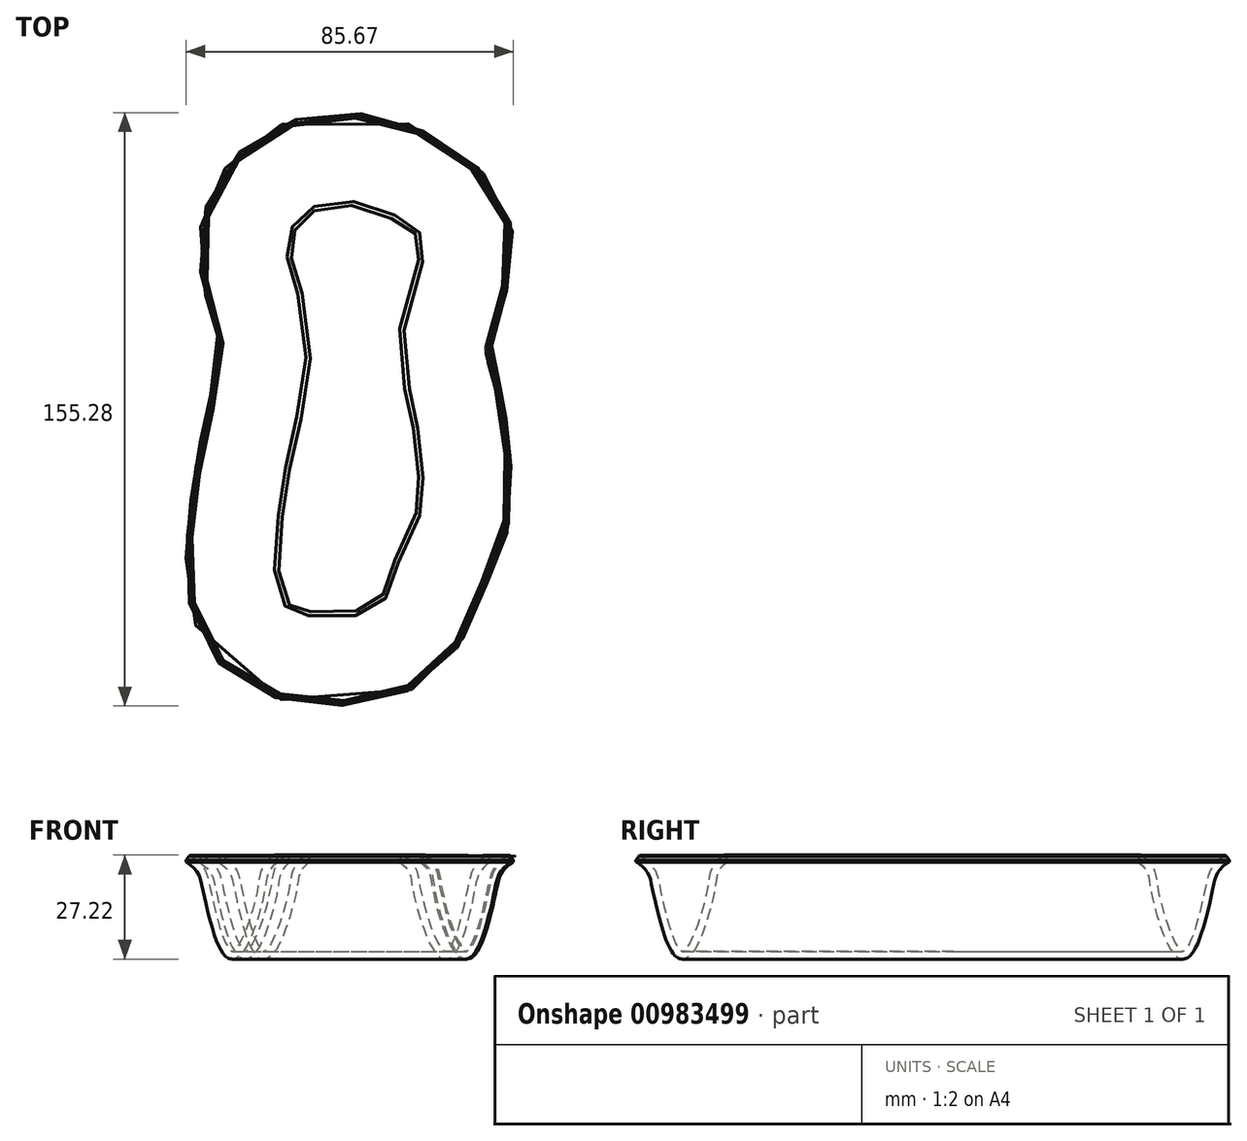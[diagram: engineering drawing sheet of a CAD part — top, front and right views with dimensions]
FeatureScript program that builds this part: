
annotation { "Feature Type Name" : "Feature", "Feature Type Description" : "" }
export const myFeature = defineFeature(function(context is Context, id is Id, definition is map)
    precondition{}
    {
        {
            var Q0;
            Q0=qCreatedBy(makeId("Top.planeOp"),FACE);
            var sketch = newSketch(context, id + "F0", { "sketchPlane" : qUnion([Q0])});
            skFitSpline(sketch, "E0", {"points": [v(28.25, 0) * mm, v(26.64, 14.63) * mm, v(31.87, 37.77) * mm, v(21.57, 52.86) * mm, v(0, 60) * mm, v(-19.3, 52.86) * mm, v(-26, 34.83) * mm, v(-21.77, 16.91) * mm, v(-22.37, 0) * mm, v(-26.08, -17.1) * mm, v(-28.78, -35.26) * mm, v(-27.37, -58.36) * mm, v(-12.12, -70) * mm, v(15, -66) * mm, v(24.45, -49.5) * mm, v(30.66, -34.33) * mm, v(30.66, -13.46) * mm, v(28.25, 0) * mm]});
            skFitSpline(sketch, "E1.0", {"points": [v(40.04, 2.28) * mm, v(39.9, 2.84) * mm, v(39.78, 3.38) * mm, v(39.6, 4.08) * mm, v(39.4, 4.9) * mm, v(39.17, 5.83) * mm, v(38.9, 7) * mm, v(38.64, 8.3) * mm, v(38.44, 9.68) * mm, v(38.38, 10.72) * mm, v(38.39, 11.53) * mm, v(38.42, 12.04) * mm, v(38.46, 12.45) * mm, v(38.5, 12.76) * mm, v(38.55, 13.08) * mm, v(38.61, 13.46) * mm, v(38.7, 13.87) * mm, v(38.83, 14.47) * mm, v(39.12, 15.64) * mm, v(39.7, 17.61) * mm, v(40.57, 20.35) * mm, v(41.54, 23.39) * mm, v(42.33, 26.16) * mm, v(42.91, 28.53) * mm, v(43.3, 30.39) * mm, v(43.62, 32.34) * mm, v(43.8, 34.06) * mm, v(43.88, 35.49) * mm, v(43.91, 36.58) * mm, v(43.9, 37.52) * mm, v(43.86, 38.29) * mm, v(43.81, 39.06) * mm, v(43.72, 40.02) * mm, v(43.5, 41.54) * mm, v(43.11, 43.4) * mm, v(42.47, 45.53) * mm, v(41.68, 47.57) * mm, v(40.76, 49.5) * mm, v(39.37, 51.91) * mm, v(37.41, 54.65) * mm, v(34.8, 57.53) * mm, v(32.03, 60.05) * mm, v(29.62, 61.9) * mm, v(27.66, 63.24) * mm, v(26.16, 64.2) * mm, v(24.61, 65.12) * mm, v(22.5, 66.28) * mm, v(19.8, 67.6) * mm, v(15.28, 69.43) * mm, v(10.53, 70.82) * mm, v(5.6, 71.66) * mm, v(1.8, 72) * mm, v(-2.06, 72.02) * mm, v(-5.9, 71.7) * mm, v(-9.7, 71.05) * mm, v(-13.45, 70.03) * mm, v(-17.12, 68.65) * mm, v(-20.67, 66.87) * mm, v(-23.5, 65.03) * mm, v(-25.64, 63.34) * mm, v(-27.19, 61.96) * mm, v(-28.66, 60.47) * mm, v(-30, 58.9) * mm, v(-31.25, 57.29) * mm, v(-32.75, 55.05) * mm, v(-34.36, 52.14) * mm, v(-35.88, 48.52) * mm, v(-37, 44.79) * mm, v(-37.61, 41.62) * mm, v(-37.9, 39.05) * mm, v(-38.02, 37.12) * mm, v(-38.03, 35.18) * mm, v(-37.94, 33.22) * mm, v(-37.74, 31.36) * mm, v(-37.39, 29) * mm, v(-36.8, 26.27) * mm, v(-36, 23.34) * mm, v(-35.2, 20.73) * mm, v(-34.62, 18.82) * mm, v(-34.22, 17.44) * mm, v(-33.97, 16.5) * mm, v(-33.8, 15.78) * mm, v(-33.67, 15.24) * mm, v(-33.6, 14.87) * mm, v(-33.53, 14.5) * mm, v(-33.45, 14.02) * mm, v(-33.37, 13.4) * mm, v(-33.3, 12.64) * mm, v(-33.24, 11.58) * mm, v(-33.22, 9.65) * mm, v(-33.4, 7.22) * mm, v(-33.75, 4.57) * mm, v(-34.05, 2.84) * mm, v(-34.31, 1.4) * mm, v(-34.6, -0.06) * mm, v(-34.99, -1.92) * mm, v(-35.5, -4.2) * mm, v(-36.02, -6.55) * mm, v(-36.57, -8.94) * mm, v(-37.13, -11.38) * mm, v(-37.58, -13.45) * mm, v(-37.93, -15.14) * mm, v(-38.26, -16.83) * mm, v(-38.66, -18.94) * mm, v(-39.24, -22.34) * mm, v(-39.75, -25.8) * mm, v(-40.2, -29.37) * mm, v(-40.47, -31.68) * mm, v(-40.67, -33.56) * mm, v(-40.86, -35.49) * mm, v(-41.1, -38.05) * mm, v(-41.32, -41.3) * mm, v(-41.44, -44.7) * mm, v(-41.41, -48.23) * mm, v(-41.18, -51.87) * mm, v(-40.75, -55) * mm, v(-40.22, -57.54) * mm, v(-39.71, -59.47) * mm, v(-39.19, -61.1) * mm, v(-38.7, -62.4) * mm, v(-38.15, -63.7) * mm, v(-37.39, -65.3) * mm, v(-36.34, -67.13) * mm, v(-35.17, -68.9) * mm, v(-33.45, -71.1) * mm, v(-31.03, -73.63) * mm, v(-27.77, -76.2) * mm, v(-24.23, -78.34) * mm, v(-20.49, -80.03) * mm, v(-16.58, -81.32) * mm, v(-12.53, -82.22) * mm, v(-8.4, -82.79) * mm, v(-4.21, -83.02) * mm, v(0.01, -82.94) * mm, v(4.25, -82.53) * mm, v(8.47, -81.77) * mm, v(12.65, -80.6) * mm, v(16.07, -79.25) * mm, v(18.42, -78.05) * mm, v(19.74, -77.28) * mm, v(20.72, -76.66) * mm, v(21.68, -76) * mm, v(22.64, -75.27) * mm, v(23.55, -74.52) * mm, v(24.7, -73.49) * mm, v(26.02, -72.15) * mm, v(27.42, -70.5) * mm, v(28.65, -68.83) * mm, v(30.08, -66.61) * mm, v(31.53, -63.92) * mm, v(32.64, -61.4) * mm, v(33.4, -59.54) * mm, v(33.92, -58.22) * mm, v(34.39, -56.99) * mm, v(34.75, -56.04) * mm, v(35.02, -55.34) * mm, v(35.22, -54.84) * mm, v(35.41, -54.37) * mm, v(35.6, -53.94) * mm, v(35.79, -53.5) * mm, v(36.05, -52.89) * mm, v(36.4, -52.12) * mm, v(36.87, -51.15) * mm, v(37.52, -49.8) * mm, v(38.4, -47.98) * mm, v(39.53, -45.54) * mm, v(40.47, -43.25) * mm, v(41.18, -41.25) * mm, v(41.68, -39.67) * mm, v(42.06, -38.29) * mm, v(42.33, -37.14) * mm, v(42.58, -35.97) * mm, v(42.83, -34.53) * mm, v(43.07, -32.8) * mm, v(43.25, -31.1) * mm, v(43.42, -28.84) * mm, v(43.5, -26.06) * mm, v(43.46, -22.8) * mm, v(43.3, -19.65) * mm, v(43.07, -16.62) * mm, v(42.83, -14.23) * mm, v(42.62, -12.42) * mm, v(42.4, -10.68) * mm, v(42.12, -8.58) * mm, v(41.75, -6.18) * mm, v(41.35, -3.85) * mm, v(40.98, -1.96) * mm, v(40.67, -0.48) * mm, v(40.43, 0.63) * mm, v(40.22, 1.55) * mm, v(40.04, 2.28) * mm, v(39.9, 2.84) * mm, v(39.78, 3.38) * mm, v(40.04, 2.28) * mm]});
            skFitSpline(sketch, "E2.0", {"points": [v(16.7, -3.29) * mm, v(16.59, -2.84) * mm, v(16.48, -2.38) * mm, v(16.32, -1.73) * mm, v(16.1, -0.87) * mm, v(15.83, 0.26) * mm, v(15.45, 1.87) * mm, v(15, 4.11) * mm, v(14.63, 6.64) * mm, v(14.44, 8.83) * mm, v(14.38, 10.55) * mm, v(14.39, 12.33) * mm, v(14.48, 13.87) * mm, v(14.6, 15.13) * mm, v(14.73, 16.1) * mm, v(14.87, 17.06) * mm, v(15.04, 17.99) * mm, v(15.23, 18.9) * mm, v(15.5, 20.08) * mm, v(16, 22.08) * mm, v(16.78, 24.75) * mm, v(17.73, 27.71) * mm, v(18.59, 30.42) * mm, v(19.16, 32.43) * mm, v(19.5, 33.83) * mm, v(19.7, 34.77) * mm, v(19.82, 35.58) * mm, v(19.88, 36.13) * mm, v(19.9, 36.49) * mm, v(19.9, 36.71) * mm, v(19.9, 36.86) * mm, v(19.9, 36.96) * mm, v(19.9, 37.04) * mm, v(19.88, 37.14) * mm, v(19.86, 37.3) * mm, v(19.82, 37.48) * mm, v(19.75, 37.73) * mm, v(19.6, 38.1) * mm, v(19.32, 38.66) * mm, v(18.72, 39.51) * mm, v(17.84, 40.5) * mm, v(16.66, 41.58) * mm, v(15.46, 42.5) * mm, v(14.39, 43.24) * mm, v(13.56, 43.77) * mm, v(12.7, 44.28) * mm, v(11.52, 44.93) * mm, v(10, 45.67) * mm, v(7.51, 46.68) * mm, v(4.97, 47.41) * mm, v(2.47, 47.84) * mm, v(0.94, 47.98) * mm, v(-0.24, 48) * mm, v(-1.41, 47.99) * mm, v(-2.86, 47.87) * mm, v(-4.53, 47.58) * mm, v(-6.08, 47.16) * mm, v(-7.49, 46.62) * mm, v(-8.73, 46) * mm, v(-9.6, 45.42) * mm, v(-10.22, 44.94) * mm, v(-10.63, 44.57) * mm, v(-11, 44.2) * mm, v(-11.37, 43.77) * mm, v(-11.73, 43.3) * mm, v(-12.19, 42.61) * mm, v(-12.72, 41.66) * mm, v(-13.25, 40.4) * mm, v(-13.66, 39.04) * mm, v(-13.88, 37.9) * mm, v(-13.98, 36.99) * mm, v(-14.02, 36.32) * mm, v(-14.02, 35.68) * mm, v(-14, 35.07) * mm, v(-13.93, 34.4) * mm, v(-13.78, 33.41) * mm, v(-13.49, 32.01) * mm, v(-12.96, 30.06) * mm, v(-12.3, 27.85) * mm, v(-11.65, 25.77) * mm, v(-11.12, 23.96) * mm, v(-10.73, 22.53) * mm, v(-10.42, 21.26) * mm, v(-10.2, 20.2) * mm, v(-10.03, 19.4) * mm, v(-9.87, 18.56) * mm, v(-9.7, 17.46) * mm, v(-9.52, 16.09) * mm, v(-9.36, 14.46) * mm, v(-9.24, 12.32) * mm, v(-9.21, 9.71) * mm, v(-9.36, 6.68) * mm, v(-9.64, 3.75) * mm, v(-10.03, 0.93) * mm, v(-10.4, -1.33) * mm, v(-10.74, -3.1) * mm, v(-11.08, -4.84) * mm, v(-11.52, -6.98) * mm, v(-12.08, -9.49) * mm, v(-12.63, -11.93) * mm, v(-13.18, -14.3) * mm, v(-13.7, -16.6) * mm, v(-14.1, -18.47) * mm, v(-14.4, -19.92) * mm, v(-14.7, -21.36) * mm, v(-15.03, -23.16) * mm, v(-15.53, -26.07) * mm, v(-15.97, -29.07) * mm, v(-16.32, -31.84) * mm, v(-16.52, -33.48) * mm, v(-16.66, -34.74) * mm, v(-16.8, -36.03) * mm, v(-16.97, -37.8) * mm, v(-17.17, -40) * mm, v(-17.35, -42.58) * mm, v(-17.44, -45.07) * mm, v(-17.41, -47.4) * mm, v(-17.27, -49.52) * mm, v(-17.06, -51.03) * mm, v(-16.84, -52.06) * mm, v(-16.66, -52.74) * mm, v(-16.5, -53.21) * mm, v(-16.38, -53.54) * mm, v(-16.26, -53.83) * mm, v(-16.1, -54.16) * mm, v(-15.9, -54.52) * mm, v(-15.67, -54.86) * mm, v(-15.34, -55.28) * mm, v(-14.85, -55.8) * mm, v(-14.1, -56.4) * mm, v(-13.1, -57.02) * mm, v(-11.81, -57.6) * mm, v(-10.49, -58.05) * mm, v(-9.28, -58.35) * mm, v(-7.96, -58.62) * mm, v(-6.13, -58.87) * mm, v(-3.77, -59) * mm, v(-1.36, -58.96) * mm, v(0.98, -58.73) * mm, v(3.16, -58.33) * mm, v(5.05, -57.8) * mm, v(6.3, -57.3) * mm, v(6.96, -56.95) * mm, v(7.27, -56.77) * mm, v(7.47, -56.64) * mm, v(7.64, -56.52) * mm, v(7.77, -56.42) * mm, v(7.9, -56.32) * mm, v(8.07, -56.16) * mm, v(8.29, -55.94) * mm, v(8.66, -55.5) * mm, v(9.2, -54.75) * mm, v(9.91, -53.43) * mm, v(10.56, -52) * mm, v(11.1, -50.68) * mm, v(11.52, -49.6) * mm, v(11.96, -48.44) * mm, v(12.35, -47.41) * mm, v(12.69, -46.56) * mm, v(12.95, -45.9) * mm, v(13.22, -45.22) * mm, v(13.52, -44.52) * mm, v(13.8, -43.85) * mm, v(14.2, -42.98) * mm, v(14.67, -41.94) * mm, v(15.23, -40.76) * mm, v(15.94, -39.3) * mm, v(16.75, -37.63) * mm, v(17.55, -35.88) * mm, v(18.08, -34.58) * mm, v(18.43, -33.62) * mm, v(18.65, -32.92) * mm, v(18.8, -32.34) * mm, v(18.9, -31.89) * mm, v(19, -31.42) * mm, v(19.12, -30.78) * mm, v(19.28, -29.64) * mm, v(19.43, -28.02) * mm, v(19.5, -25.87) * mm, v(19.47, -23.57) * mm, v(19.35, -21.19) * mm, v(19.17, -18.79) * mm, v(18.97, -16.81) * mm, v(18.79, -15.27) * mm, v(18.6, -13.77) * mm, v(18.36, -12) * mm, v(18.06, -10.04) * mm, v(17.74, -8.18) * mm, v(17.45, -6.7) * mm, v(17.2, -5.5) * mm, v(17, -4.62) * mm, v(16.84, -3.88) * mm, v(16.7, -3.29) * mm, v(16.59, -2.84) * mm, v(16.48, -2.38) * mm, v(16.7, -3.29) * mm]});
            skSolve(sketch);
        }
        {
            var Q0;
            Q0=qCreatedBy(makeId("Front.planeOp"),FACE);
            var sketch = newSketch(context, id + "F1", { "sketchPlane" : qUnion([Q0])});
            skPoint(sketch, "E3.0", {"position": v(28.25, 0) * mm});
            skPoint(sketch, "E4.0", {"position": v(-22.37, 0) * mm});
            skLineSegment(sketch, "E5", {"start": v(28.25, 0) * mm, "end": v(28.25, -25.4) * mm, "construction": true});
            skLineSegment(sketch, "E6", {"start": v(-22.37, 0) * mm, "end": v(-22.37, -25.4) * mm, "construction": true});
            skFitSpline(sketch, "E7", {"points": [v(16.25, 0) * mm, v(20.42, -7.94) * mm, v(28.25, -25.4) * mm, v(35.13, -8.3) * mm, v(40.25, 0) * mm], "startDerivative": vector(56.27, -41.27) * mm, "endDerivative": vector(56.95, 39.57) * mm, "construction": true});
            skFitSpline(sketch, "E8.0", {"points": [v(15.66, -0.8) * mm, v(16.22, -1.22) * mm, v(17.14, -1.96) * mm, v(18, -2.88) * mm, v(18.48, -3.7) * mm, v(18.8, -4.58) * mm, v(18.98, -5.53) * mm, v(19.14, -6.46) * mm, v(19.27, -7.26) * mm, v(19.43, -8.15) * mm, v(19.7, -9.47) * mm, v(20.14, -11.32) * mm, v(20.8, -13.74) * mm, v(21.57, -16.25) * mm, v(22.44, -18.72) * mm, v(23.4, -21.04) * mm, v(24.24, -22.75) * mm, v(24.94, -23.93) * mm, v(25.5, -24.71) * mm, v(26.08, -25.38) * mm, v(26.72, -25.92) * mm, v(27.34, -26.25) * mm, v(27.9, -26.39) * mm, v(28.35, -26.41) * mm, v(28.78, -26.35) * mm, v(29.32, -26.16) * mm, v(29.9, -25.8) * mm, v(30.5, -25.2) * mm, v(31.03, -24.5) * mm, v(31.52, -23.69) * mm, v(32.14, -22.47) * mm, v(32.85, -20.73) * mm, v(33.64, -18.4) * mm, v(34.36, -15.93) * mm, v(35, -13.44) * mm, v(35.56, -11.06) * mm, v(35.95, -9.28) * mm, v(36.22, -8.03) * mm, v(36.46, -6.91) * mm, v(36.73, -5.75) * mm, v(37.1, -4.66) * mm, v(37.57, -3.76) * mm, v(38.25, -2.9) * mm, v(39.26, -1.95) * mm, v(40.24, -1.22) * mm, v(40.82, -0.82) * mm]});
            skFitSpline(sketch, "E9.0", {"points": [v(16.84, 0.8) * mm, v(17.45, 0.36) * mm, v(18.47, -0.46) * mm, v(19.57, -1.63) * mm, v(20.31, -2.84) * mm, v(20.74, -4.1) * mm, v(21, -5.4) * mm, v(21.2, -6.63) * mm, v(21.4, -7.77) * mm, v(21.6, -8.71) * mm, v(21.83, -9.75) * mm, v(22.19, -11.22) * mm, v(22.72, -13.19) * mm, v(23.47, -15.63) * mm, v(24.32, -18.02) * mm, v(25.22, -20.23) * mm, v(26, -21.81) * mm, v(26.63, -22.84) * mm, v(27.08, -23.48) * mm, v(27.5, -23.97) * mm, v(27.88, -24.27) * mm, v(28.1, -24.38) * mm, v(28.2, -24.4) * mm, v(28.25, -24.4) * mm, v(28.3, -24.4) * mm, v(28.41, -24.36) * mm, v(28.63, -24.24) * mm, v(28.97, -23.9) * mm, v(29.36, -23.4) * mm, v(29.76, -22.72) * mm, v(30.3, -21.66) * mm, v(30.97, -20.04) * mm, v(31.73, -17.8) * mm, v(32.43, -15.4) * mm, v(33.05, -12.96) * mm, v(33.6, -10.62) * mm, v(34, -8.85) * mm, v(34.26, -7.6) * mm, v(34.5, -6.48) * mm, v(34.8, -5.23) * mm, v(35.24, -3.9) * mm, v(35.88, -2.66) * mm, v(36.8, -1.5) * mm, v(38, -0.4) * mm, v(39.07, 0.4) * mm, v(39.68, 0.82) * mm]});
            skLineSegment(sketch, "E10", {"start": v(16.84, 0.8) * mm, "end": v(15.66, -0.8) * mm});
            skLineSegment(sketch, "E11", {"start": v(39.68, 0.82) * mm, "end": v(40.82, -0.82) * mm});
            skSolve(sketch);
        }
        {
            var Q0;
            Q0=makeQuery(id+"F1.imprint","IMPRINT",FACE,{"disambiguationData":[TD([[makeQuery(id+"F1.imprint","IMPRINT",EDGE,{"derivedFrom":sQuery(id+"F1.wireOp",EDGE,"E8.0")}),1.0]])]});
            var Q1;
            Q1=sQuery(id+"F0.wireOp",EDGE,"E0");
            sweep(context, id + "F2", {"profiles" : qUnion([Q0]), "path" : qUnion([Q1])});
        }
        {
            var Q0;
            Q0=makeQuery(id+"F2.opSweep","SWEPT_EDGE",EDGE,{"disambiguationData":[OSD([sQuery(id+"F0.wireOp",EDGE,"E0"),sQuery(id+"F1.wireOp",EDGE,"E8.0"),sQuery(id+"F1.wireOp",EDGE,"E11")])]});
            var Q1;
            Q1=makeQuery(id+"F2.opSweep","SWEPT_EDGE",EDGE,{"disambiguationData":[OSD([sQuery(id+"F0.wireOp",EDGE,"E0"),sQuery(id+"F1.wireOp",EDGE,"E9.0"),sQuery(id+"F1.wireOp",EDGE,"E11")])]});
            fillet(context, id + "F3", {"entities" : qUnion([Q0, Q1]), "radius" : .4 * mm, "tangentPropagation" : true, "allowEdgeOverflow" : false});
        }
    });
